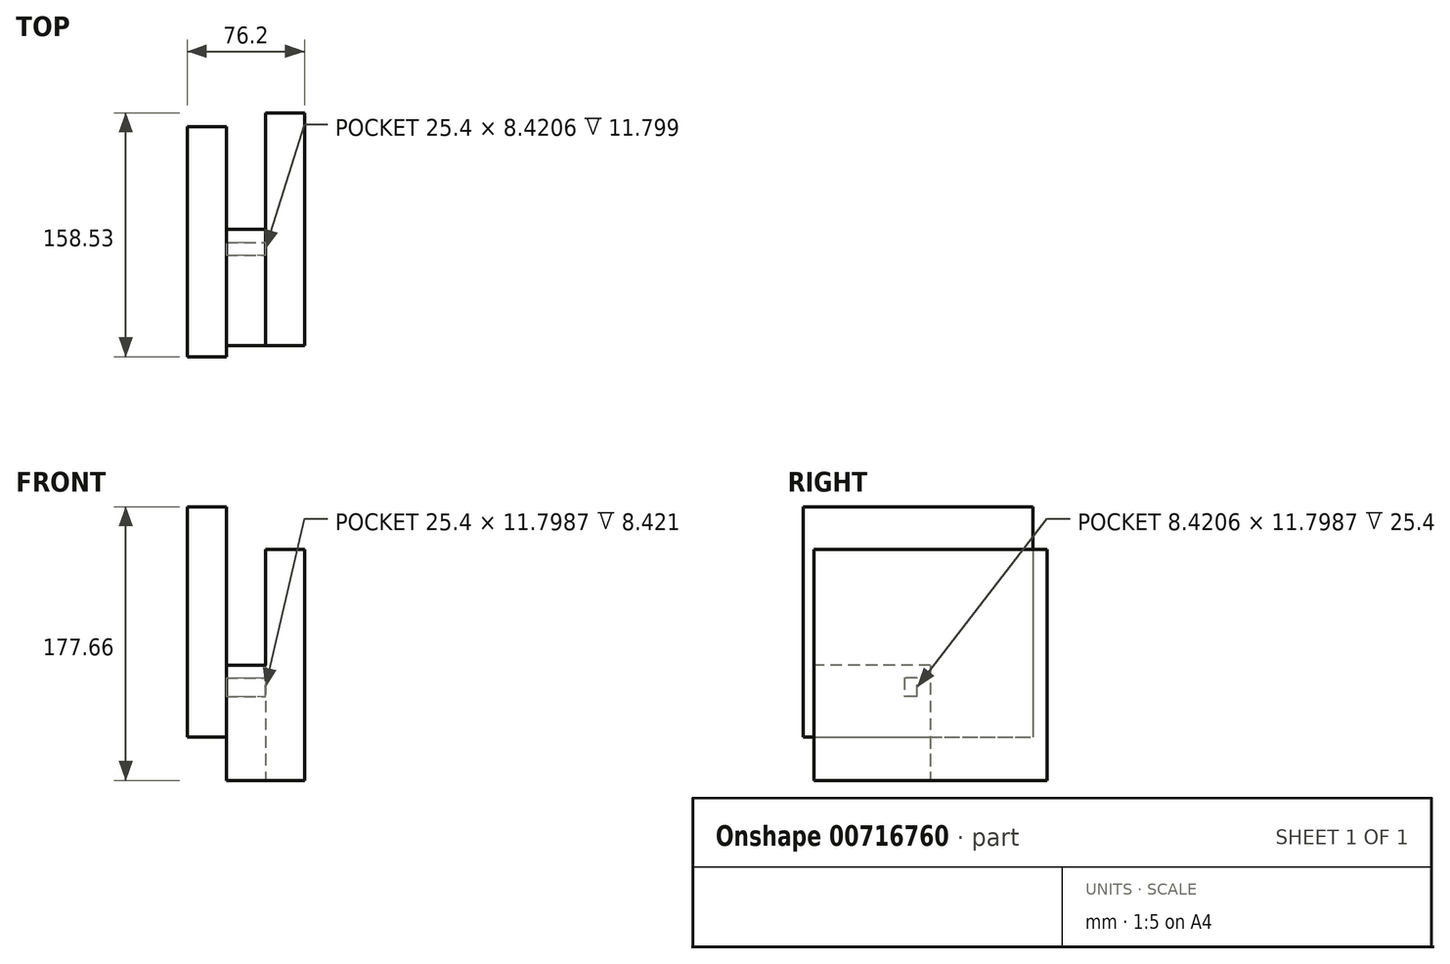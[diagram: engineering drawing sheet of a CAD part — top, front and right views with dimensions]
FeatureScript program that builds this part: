
annotation { "Feature Type Name" : "Feature", "Feature Type Description" : "" }
export const myFeature = defineFeature(function(context is Context, id is Id, definition is map)
    precondition{}
    {
        {
            var Q0;
            Q0=qCreatedBy(makeId("Right.planeOp"),FACE);
            var sketch = newSketch(context, id + "F0", { "sketchPlane" : qUnion([Q0])});
            skLineSegment(sketch, "E0.bottom", {"start": v(-75.59, 75.17) * mm, "end": v(75.7, 75.17) * mm});
            skLineSegment(sketch, "E0.top", {"start": v(-75.59, -74.71) * mm, "end": v(75.7, -74.71) * mm});
            skLineSegment(sketch, "E0.left", {"start": v(-75.59, 75.17) * mm, "end": v(-75.59, -74.71) * mm});
            skLineSegment(sketch, "E0.right", {"start": v(75.7, 75.17) * mm, "end": v(75.7, -74.71) * mm});
            skLineSegment(sketch, "E1.bottom", {"start": v(0, 0) * mm, "end": v(-75.59, 0) * mm});
            skLineSegment(sketch, "E1.top", {"start": v(0, 75.17) * mm, "end": v(-75.59, 75.17) * mm});
            skLineSegment(sketch, "E1.left", {"start": v(0, 0) * mm, "end": v(0, 75.17) * mm});
            skLineSegment(sketch, "E1.right", {"start": v(-75.59, 0) * mm, "end": v(-75.59, 75.17) * mm});
            skLineSegment(sketch, "E2.bottom", {"start": v(-75.59, 0) * mm, "end": v(75.7, 0) * mm});
            skLineSegment(sketch, "E2.left", {"start": v(-75.59, 0) * mm, "end": v(-75.59, -74.71) * mm});
            skLineSegment(sketch, "E2.right", {"start": v(75.7, 0) * mm, "end": v(75.7, -74.71) * mm});
            skLineSegment(sketch, "E3.bottom", {"start": v(75.7, 0) * mm, "end": v(0, 0) * mm});
            skLineSegment(sketch, "E3.top", {"start": v(75.7, 75.17) * mm, "end": v(0, 75.17) * mm});
            skLineSegment(sketch, "E3.left", {"start": v(75.7, 0) * mm, "end": v(75.7, 75.17) * mm});
            skSolve(sketch);
        }
        {
            var Q0;
            Q0 = qSketchRegion(id + "F0", true);
            extrude(context, id + "F1", {"entities" : qUnion([Q0]), "depth" : 25.4 * mm, "offsetDistance" : 25.4 * mm});
        }
        {
            var Q0;
            Q0=makeQuery(id+"F1.opExtrude","CAP_FACE",FACE,{"disambiguationData":[OSD([sQuery(id+"F0.wireOp",EDGE,"E1.top"),sQuery(id+"F0.wireOp",EDGE,"E1.right"),sQuery(id+"F0.wireOp",EDGE,"E0.top"),sQuery(id+"F0.wireOp",EDGE,"E2.left"),sQuery(id+"F0.wireOp",EDGE,"E2.right"),sQuery(id+"F0.wireOp",EDGE,"E3.top"),sQuery(id+"F0.wireOp",EDGE,"E3.left")])],"isStart":true});
            var sketch = newSketch(context, id + "F2", { "sketchPlane" : qUnion([Q0])});
            skLineSegment(sketch, "E4.bottom", {"start": v(75.59, -74.71) * mm, "end": v(17, -74.71) * mm});
            skLineSegment(sketch, "E4.top", {"start": v(75.59, -33.12) * mm, "end": v(17, -33.12) * mm});
            skLineSegment(sketch, "E4.left", {"start": v(75.59, -74.71) * mm, "end": v(75.59, -33.12) * mm});
            skLineSegment(sketch, "E4.right", {"start": v(17, -74.71) * mm, "end": v(17, -33.12) * mm});
            skLineSegment(sketch, "E5.bottom", {"start": v(0, -8.32) * mm, "end": v(17, -8.32) * mm});
            skLineSegment(sketch, "E5.top", {"start": v(0, -22.45) * mm, "end": v(17, -22.45) * mm});
            skLineSegment(sketch, "E5.left", {"start": v(0, -8.32) * mm, "end": v(0, -22.45) * mm});
            skLineSegment(sketch, "E5.right", {"start": v(17, -8.32) * mm, "end": v(17, -22.45) * mm});
            skPoint(sketch, "E6.oppositeSnap0", {"position": v(75.59, 0.23) * mm});
            skLineSegment(sketch, "E6.bottom", {"start": v(8.58, -20.12) * mm, "end": v(75.59, -20.12) * mm});
            skLineSegment(sketch, "E6.top", {"start": v(8.58, 0) * mm, "end": v(75.59, 0) * mm});
            skLineSegment(sketch, "E6.left", {"start": v(8.58, -20.12) * mm, "end": v(8.58, 0) * mm});
            skLineSegment(sketch, "E6.right", {"start": v(75.59, -20.12) * mm, "end": v(75.59, 0) * mm});
            skLineSegment(sketch, "E7.bottom", {"start": v(0, 0) * mm, "end": v(8.58, 0) * mm});
            skLineSegment(sketch, "E7.top", {"start": v(0, 0) * mm, "end": v(8.58, 0) * mm});
            skLineSegment(sketch, "E7.left", {"start": v(0, 0) * mm, "end": v(0, 0) * mm});
            skLineSegment(sketch, "E7.right", {"start": v(8.58, 0) * mm, "end": v(8.58, 0) * mm});
            skLineSegment(sketch, "E8.bottom", {"start": v(0, 0) * mm, "end": v(17, 0) * mm});
            skLineSegment(sketch, "E8.top", {"start": v(0, -74.71) * mm, "end": v(17, -74.71) * mm});
            skLineSegment(sketch, "E8.left", {"start": v(0, 0) * mm, "end": v(0, -74.71) * mm});
            skLineSegment(sketch, "E8.right", {"start": v(17, 0) * mm, "end": v(17, -74.71) * mm});
            skLineSegment(sketch, "E9.bottom", {"start": v(75.59, -20.12) * mm, "end": v(75.59, -20.12) * mm});
            skLineSegment(sketch, "E9.top", {"start": v(75.59, -33.12) * mm, "end": v(75.59, -33.12) * mm});
            skLineSegment(sketch, "E9.left", {"start": v(75.59, -20.12) * mm, "end": v(75.59, -33.12) * mm});
            skLineSegment(sketch, "E9.right", {"start": v(75.59, -20.12) * mm, "end": v(75.59, -33.12) * mm});
            skSolve(sketch);
        }
        {
            var Q0;
            Q0 = qSketchRegion(id + "F2", true);
            extrude(context, id + "F3", {"entities" : qUnion([Q0]), "operationType" : NewBodyOperationType.ADD, "depth" : 25.4 * mm, "offsetDistance" : 25.4 * mm});
        }
        {
            var Q0;
            Q0=makeQuery(id+"F3.opExtrude","CAP_FACE",FACE,{"disambiguationData":[OSD([sQuery(id+"F2.wireOp",EDGE,"E4.bottom"),sQuery(id+"F2.wireOp",EDGE,"E4.left"),sQuery(id+"F2.wireOp",EDGE,"E5.bottom"),sQuery(id+"F2.wireOp",EDGE,"E6.bottom"),sQuery(id+"F2.wireOp",EDGE,"E6.top"),sQuery(id+"F2.wireOp",EDGE,"E6.left"),sQuery(id+"F2.wireOp",EDGE,"E6.right"),sQuery(id+"F2.wireOp",EDGE,"E8.bottom"),sQuery(id+"F2.wireOp",EDGE,"E8.top"),sQuery(id+"F2.wireOp",EDGE,"E8.left"),sQuery(id+"F2.wireOp",EDGE,"E8.right"),sQuery(id+"F2.wireOp",EDGE,"E9.right")])],"isStart":false});
            var sketch = newSketch(context, id + "F4", { "sketchPlane" : qUnion([Q0])});
            skLineSegment(sketch, "E10.bottom", {"start": v(24.64, 94.38) * mm, "end": v(-66.51, 94.38) * mm});
            skLineSegment(sketch, "E10.top", {"start": v(24.64, -46.7) * mm, "end": v(-66.51, -46.7) * mm});
            skLineSegment(sketch, "E10.left", {"start": v(24.64, 94.38) * mm, "end": v(24.64, -46.7) * mm});
            skLineSegment(sketch, "E10.right", {"start": v(-66.51, 94.38) * mm, "end": v(-66.51, -46.7) * mm});
            skLineSegment(sketch, "E11.bottom", {"start": v(24.64, -46.7) * mm, "end": v(82.84, -46.7) * mm});
            skLineSegment(sketch, "E11.top", {"start": v(24.64, 102.95) * mm, "end": v(82.84, 102.95) * mm});
            skLineSegment(sketch, "E11.left", {"start": v(24.64, -46.7) * mm, "end": v(24.64, 102.95) * mm});
            skLineSegment(sketch, "E11.right", {"start": v(82.84, -46.7) * mm, "end": v(82.84, 102.95) * mm});
            skLineSegment(sketch, "E12.bottom", {"start": v(24.64, 102.95) * mm, "end": v(-66.51, 102.95) * mm});
            skLineSegment(sketch, "E12.left", {"start": v(24.64, 102.95) * mm, "end": v(24.64, 94.38) * mm});
            skLineSegment(sketch, "E12.right", {"start": v(-66.51, 102.95) * mm, "end": v(-66.51, 94.38) * mm});
            skSolve(sketch);
        }
        {
            var Q0;
            Q0 = qSketchRegion(id + "F4", true);
            extrude(context, id + "F5", {"entities" : qUnion([Q0]), "operationType" : NewBodyOperationType.ADD, "depth" : 25.4 * mm, "offsetDistance" : 25.4 * mm});
        }
    });
